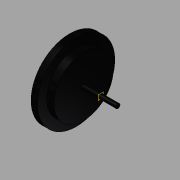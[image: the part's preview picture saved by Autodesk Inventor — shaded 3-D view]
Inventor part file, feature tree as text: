
AUTODESK INVENTOR PART (.ipt)
format: ipt  version: 2015 (Build 190159000, 159)  size: 141,824 bytes
history: native  units: in
note: dims shown in document units (in); Inventor stores cm internally (conversion verified against a paired STEP export)
features: sketch x5, other x3, plane x1
ambient origin geometry x8: Origin, YZ Plane, XZ Plane, XY Plane, X Axis, Y Axis, Z Axis, Center Point
bodies: Solid1 (feature_tree)
feature tree (9):
  other  "rueda_MIR3.ipt"
  other  "Solid1::rueda_MIR3.ipt"
  other  "TaggingFeature1"
  sketch  "Sketch2"  dims[d0=0.3937in]
  sketch  "Sketch3"
  sketch  "Sketch7"
  sketch  "Sketch12"
  sketch  "Sketch13"
  plane  "Work Plane1"
